# Revit family: Access_Door_ACUDOR_Flush-Drywall_DW-5040
name_source: partatom
category: Doors
revit_build: Autodesk Revit 2017 (Build: 20171027_0315(x64)
units: mm (PartAtom-declared; Revit-internal decimal feet)

## family parameters
Cut with Voids When Loaded = No
Host = Face
Room Calculation Point = No
Shared = No

## types (12) — shared parameters
Analytic Construction = <None>
Default Elevation = 48 "
Description = FLUSH FOR DRYWALL
Manufacturer = ACUDOR
Material Finish = Metal - Acudor - Stainless - Polished
URL = www.acudor.com
zero-valued in all types: Thickness, Wall Offset

## per-type parameters (varying)
| type | Code | Height | Model | Width |
| DW-5040-0606 | 1 | 8.57 " | DW-5040-0606 | 8.57 " |
| DW-5040-0808 | 1 | 10.57 " | DW-5040-0808 | 10.57 " |
| DW-5040-1010 | 1 | 12.57 " | DW-5040-1010 | 12.57 " |
| DW-5040-1212 | 1 | 14.57 " | DW-5040-1212 | 14.57 " |
| DW-5040-1414 | 1 | 16.57 " | DW-5040-1414 | 16.57 " |
| DW-5040-1616 | 1 | 18.57 " | DW-5040-1616 | 18.57 " |
| DW-5040-1818 | 1 | 20.57 " | DW-5040-1818 | 20.57 " |
| DW-5040-2222 | 1 | 24.57 " | DW-5040-2222 | 24.57 " |
| DW-5040-2424 | 1 | 26.57 " | DW-5040-2424 | 26.57 " |
| DW-5040-2436 | 2 | 38.57 " | DW-5040-2436 | 26.57 " |
| DW-5040-3030 | 2 | 32.57 " | DW-5040-3030 | 32.57 " |
| DW-5040-3636 | 2 | 38.57 " | DW-5040-3030 | 38.57 " |

## geometry (parser evidence)
native form markers: Blend x2, Sweep x6
no freeform markers — native parametric forms only
